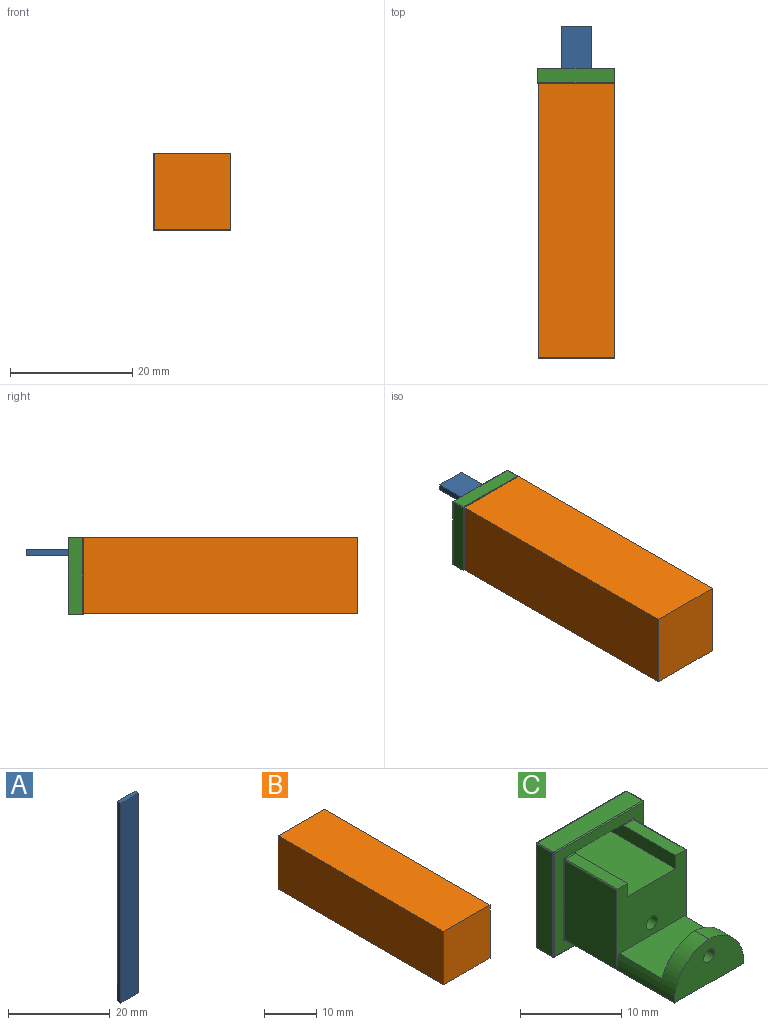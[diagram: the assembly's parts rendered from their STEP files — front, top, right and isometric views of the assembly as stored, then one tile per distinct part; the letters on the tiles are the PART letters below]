
ASSEMBLY  parts=3 mates=2
PART A: 6 faces, bbox 5x1x48 mm
  f0: plane 48x5mm, normal (0,1,0), area 240mm2, adj f1,f3,f4,f5
  f1: plane 48x1mm, normal (-1,0,0), area 48mm2, adj f0,f2,f4,f5
  f2: plane 48x5mm, normal (0,-1,0), area 240mm2, adj f1,f3,f4,f5
  f3: plane 48x1mm, normal (1,0,0), area 48mm2, adj f0,f2,f4,f5
  f4: plane 5x1mm, normal (0,0,1), area 5mm2, adj f0,f1,f2,f3
  f5: plane 5x1mm, normal (0,0,-1), area 5mm2, adj f0,f1,f2,f3
PART B: 11 faces, bbox 12.5x45x12.5 mm
  f0: plane 45x12.5mm, normal (-1,0,0), area 562.5mm2, adj f1,f3,f4,f10
  f1: plane 45x12.5mm, normal (0,0,-1), area 562.5mm2, adj f0,f2,f4,f10
  f2: plane 45x12.5mm, normal (1,0,0), area 562.5mm2, adj f1,f3,f4,f10
  f3: plane 45x12.5mm, normal (0,0,1), area 562.5mm2, adj f0,f2,f4,f10
  f4: plane 12.5x12.5mm, normal (0,1,0), area 56.2mm2, adj f0,f1,f2,f3,f5,f6,f7,f8
  f5: plane 43.75x10mm, normal (1,0,0), area 437.5mm2, adj f4,f6,f8,f9
  f6: plane 43.75x10mm, normal (0,0,1), area 437.5mm2, adj f4,f5,f7,f9
  f7: plane 43.75x10mm, normal (-1,0,0), area 437.5mm2, adj f4,f6,f8,f9
  f8: plane 43.75x10mm, normal (0,0,-1), area 437.5mm2, adj f4,f5,f7,f9
  f9: plane 10x10mm, normal (0,1,0), area 100mm2, adj f5,f6,f7,f8
  f10: plane 12.5x12.5mm, normal (0,-1,0), area 156.3mm2, adj f0,f1,f2,f3
PART C: 56 faces, bbox 12.7x17.9x12.7 mm
  f0: plane 9.9x1.7mm, normal (1,0,0), area 16.1mm2, adj f5,f6,f7,f13,f48,f53
  f1: plane 9.9x1.7mm, normal (-1,0,0), area 16.1mm2, adj f5,f13,f15,f24,f48,f53
  f2: cylinder r=0.1mm len=15.3mm, axis (0,1,0), area 2.4mm2, adj f16,f17,f20,f50,f52
  f3: cylinder r=0.1mm len=15.3mm, axis (0,1,0), area 2.4mm2, adj f14,f17,f25,f49,f52
  f4: plane 9.16x6mm, normal (0,0,1), area 55mm2, adj f5,f49,f50,f51
  f5: plane 9.77x9.67mm, normal (0,-1,0), area 65mm2, adj f0,f1,f4,f6,f14,f15,f16,f18
  f6: plane 7.3x1.41mm, normal (0,0,1), area 10.3mm2, adj f0,f5,f7,f18
  f7: cylinder r=0.1mm len=1.41mm, axis (-1,0,0), area 0.2mm2, adj f0,f6,f8,f21
  f8: plane 12.5x12.5mm, normal (0,-1,0), area 56.9mm2, adj f7,f19,f20,f21,f22,f24,f25,f26
  f9: plane 12.5x2.3mm, normal (1,0,0), area 28.7mm2, adj f33,f42,f43,f47
  f10: plane 12.5x2.3mm, normal (0,0,1), area 28.7mm2, adj f34,f35,f43,f44
  f11: plane 12.5x2.3mm, normal (-1,0,0), area 28.7mm2, adj f28,f31,f35,f36
  f12: plane 12.5x2.3mm, normal (0,0,-1), area 28.7mm2, adj f31,f32,f41,f42
  f13: plane 12.5x12.5mm, normal (0,1,0), area 143mm2, adj f0,f1,f36,f41,f44,f47,f48,f53
  f14: plane 9.57x7.3mm, normal (1,0,0), area 69.9mm2, adj f3,f5,f23,f27
  f15: plane 7.3x1.41mm, normal (0,0,1), area 10.3mm2, adj f1,f5,f23,f24
  f16: plane 9.57x7.3mm, normal (-1,0,0), area 69.9mm2, adj f2,f5,f18,f19
  f17: plane 15.3x9.57mm, normal (0,0,-1), area 146.4mm2, adj f2,f3,f22,f52
  f18: cylinder r=0.1mm len=7.3mm, axis (0,1,0), area 1.1mm2, adj f5,f6,f16,f21
  f19: cylinder r=0.1mm len=9.57mm, axis (0,0,-1), area 1.5mm2, adj f8,f16,f20,f21
  f20: torus R=0.2mm, axis (0,-1,0), area 0mm2, adj f2,f8,f19,f22
  f21: torus R=0.2mm, axis (0,-1,0), area 0mm2, adj f7,f8,f18,f19
  f22: cylinder r=0.1mm len=9.57mm, axis (1,0,0), area 1.5mm2, adj f8,f17,f20,f25
  f23: cylinder r=0.1mm len=7.3mm, axis (0,1,0), area 1.1mm2, adj f5,f14,f15,f26
  f24: cylinder r=0.1mm len=1.41mm, axis (-1,0,0), area 0.2mm2, adj f1,f8,f15,f26
  f25: torus R=0.2mm, axis (0,-1,0), area 0mm2, adj f3,f8,f22,f27
  f26: torus R=0.2mm, axis (0,-1,0), area 0mm2, adj f8,f23,f24,f27
  f27: cylinder r=0.1mm len=9.57mm, axis (0,0,1), area 1.5mm2, adj f8,f14,f25,f26
  f28: cylinder r=0.1mm len=12.5mm, axis (0,0,1), area 2mm2, adj f8,f11,f29,f30
  f29: sphere r=0.1mm, area 0mm2, adj f28,f31,f32
  f30: sphere r=0.1mm, area 0mm2, adj f28,f34,f35
  f31: cylinder r=0.1mm len=2.3mm, axis (0,1,0), area 0.4mm2, adj f11,f12,f29,f37
  f32: cylinder r=0.1mm len=12.5mm, axis (-1,0,0), area 2mm2, adj f8,f12,f29,f38
  f33: cylinder r=0.1mm len=12.5mm, axis (0,0,-1), area 2mm2, adj f8,f9,f38,f39
  f34: cylinder r=0.1mm len=12.5mm, axis (1,0,0), area 2mm2, adj f8,f10,f30,f39
  f35: cylinder r=0.1mm len=2.3mm, axis (0,1,0), area 0.4mm2, adj f10,f11,f30,f40
  f36: cylinder r=0.1mm len=12.5mm, axis (0,0,-1), area 2mm2, adj f11,f13,f37,f40
  f37: sphere r=0.1mm, area 0mm2, adj f31,f36,f41
  f38: sphere r=0.1mm, area 0mm2, adj f32,f33,f42
  f39: sphere r=0.1mm, area 0mm2, adj f33,f34,f43
  f40: sphere r=0.1mm, area 0mm2, adj f35,f36,f44
  f41: cylinder r=0.1mm len=12.5mm, axis (1,0,0), area 2mm2, adj f12,f13,f37,f45
  f42: cylinder r=0.1mm len=2.3mm, axis (0,1,0), area 0.4mm2, adj f9,f12,f38,f45
  f43: cylinder r=0.1mm len=2.3mm, axis (0,1,0), area 0.4mm2, adj f9,f10,f39,f46
  f44: cylinder r=0.1mm len=12.5mm, axis (-1,0,0), area 2mm2, adj f10,f13,f40,f46
  f45: sphere r=0.1mm, area 0mm2, adj f41,f42,f47
  f46: sphere r=0.1mm, area 0mm2, adj f43,f44,f47
  f47: cylinder r=0.1mm len=12.5mm, axis (0,0,1), area 2mm2, adj f9,f13,f45,f46
  f48: plane 6.75x2.5mm, normal (0,0,-1), area 16.9mm2, adj f0,f1,f8,f13
  f49: cylinder r=5.29mm len=8mm, axis (0,-1,0), area 26.6mm2, adj f3,f4,f5,f50,f51,f52
  f50: cylinder r=5.29mm len=8mm, axis (0,-1,0), area 26.6mm2, adj f2,f4,f5,f49,f51,f52
  f51: plane 9.16x3.5mm, normal (0,1,0), area 20.9mm2, adj f4,f49,f50,f54
  f52: plane 9.77x5.37mm, normal (0,-1,0), area 38.9mm2, adj f2,f3,f17,f49,f50,f54
  f53: plane 9.9x6.75mm, normal (0,0,1), area 66.8mm2, adj f0,f1,f5,f13
  f54: cylinder r=0.75mm len=2mm, axis (0,-1,0), area 9.4mm2, adj f51,f52
  f55: cylinder r=0.75mm len=9.9mm, axis (0,-1,0), area 46.7mm2, adj f5,f13
PLACE A rot(axis=(-1,0,0),90deg) t=(-14,-46.48,-1.9)mm
PLACE B t=(-18.36,-26.33,-9.54)mm
PLACE C t=(-26.17,-69.59,-15.34)mm
MATE planar A.f0 <-> C.f53  axis (0,0,-1) through (-21.48,-22.48,-1.9)mm
MATE planar C.f35 <-> B.f4  axis (0,-1,0) through (-27.79,-7.89,1.06)mm
